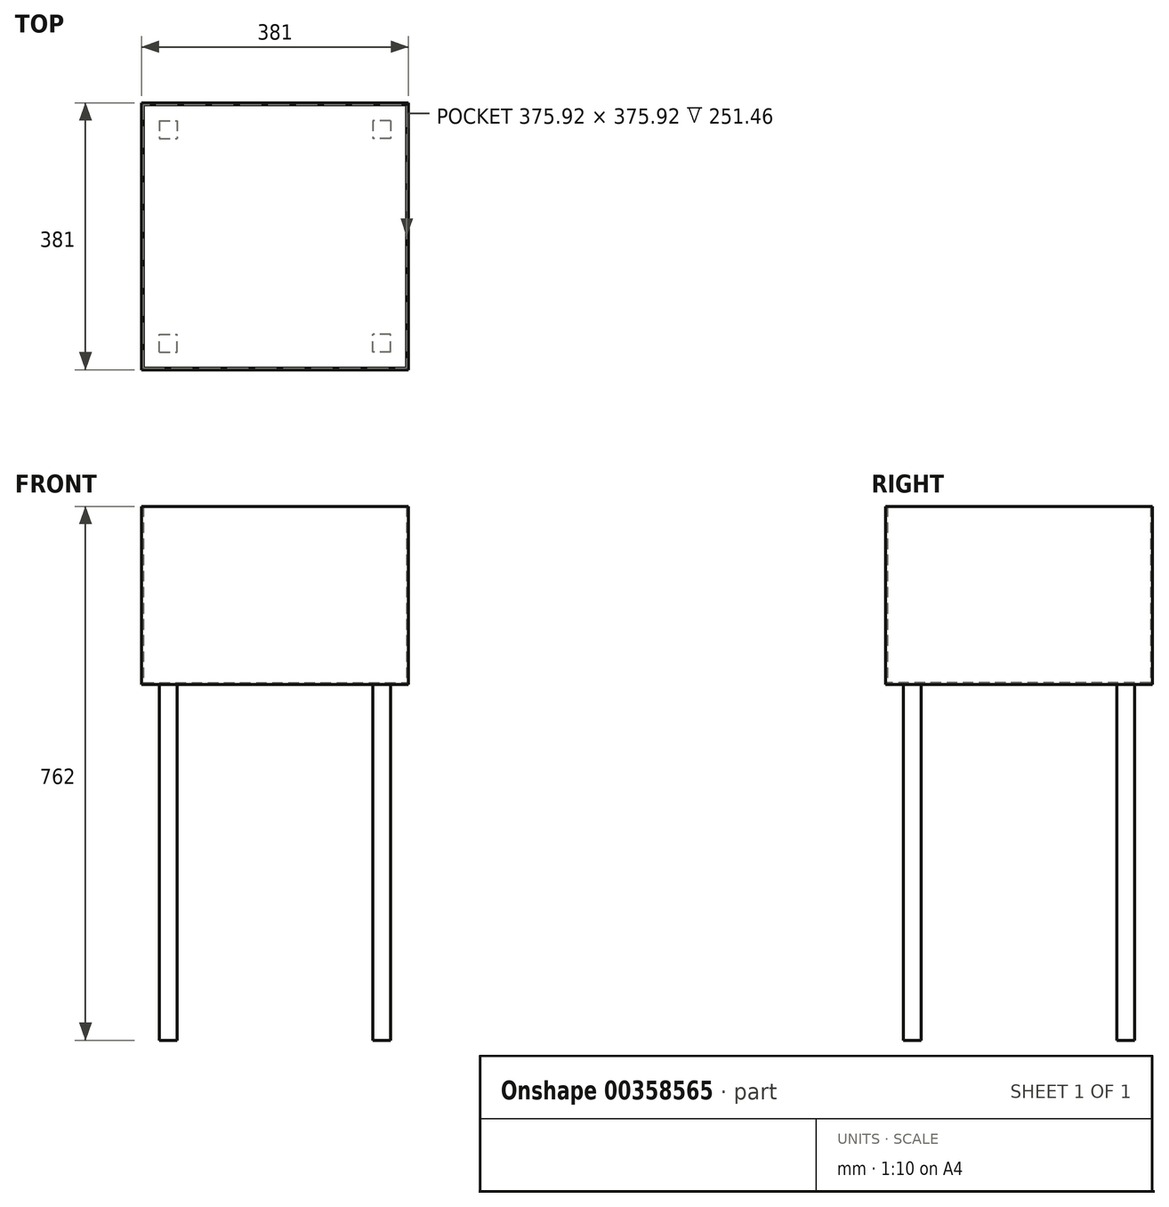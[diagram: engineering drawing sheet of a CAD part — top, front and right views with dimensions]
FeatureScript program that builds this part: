
annotation { "Feature Type Name" : "Feature", "Feature Type Description" : "" }
export const myFeature = defineFeature(function(context is Context, id is Id, definition is map)
    precondition{}
    {
        {
            var Q0;
            Q0=qCreatedBy(makeId("Top.planeOp"),FACE);
            var sketch = newSketch(context, id + "F0", { "sketchPlane" : qUnion([Q0])});
            skLineSegment(sketch, "E0.bottom", {"start": v(0, 0) * mm, "end": v(381, 0) * mm});
            skLineSegment(sketch, "E0.top", {"start": v(0, -381) * mm, "end": v(381, -381) * mm});
            skLineSegment(sketch, "E0.left", {"start": v(0, 0) * mm, "end": v(0, -381) * mm});
            skLineSegment(sketch, "E0.right", {"start": v(381, 0) * mm, "end": v(381, -381) * mm});
            skSolve(sketch);
        }
        {
            var Q0;
            Q0 = qSketchRegion(id + "F0", true);
            extrude(context, id + "F1", {"entities" : qUnion([Q0]), "depth" : 254 * mm});
        }
        {
            var Q0;
            Q0=makeQuery(id+"F1.opExtrude","CAP_FACE",FACE,{"disambiguationData":[OSD([sQuery(id+"F0.wireOp",EDGE,"E0.bottom"),sQuery(id+"F0.wireOp",EDGE,"E0.top"),sQuery(id+"F0.wireOp",EDGE,"E0.left"),sQuery(id+"F0.wireOp",EDGE,"E0.right")])],"isStart":false});
            shell(context, id + "F2", {"entities" : qUnion([Q0]), "thickness" : 2.54 * mm});
        }
        {
            var Q0;
            Q0=makeQuery(id+"F1.opExtrude","CAP_FACE",FACE,{"disambiguationData":[OSD([sQuery(id+"F0.wireOp",EDGE,"E0.bottom"),sQuery(id+"F0.wireOp",EDGE,"E0.top"),sQuery(id+"F0.wireOp",EDGE,"E0.left"),sQuery(id+"F0.wireOp",EDGE,"E0.right")])],"isStart":true});
            var sketch = newSketch(context, id + "F3", { "sketchPlane" : qUnion([Q0])});
            skLineSegment(sketch, "E1.bottom", {"start": v(25.4, 355.6) * mm, "end": v(50.8, 355.6) * mm});
            skLineSegment(sketch, "E1.top", {"start": v(25.4, 330.2) * mm, "end": v(50.8, 330.2) * mm});
            skLineSegment(sketch, "E1.left", {"start": v(25.4, 355.6) * mm, "end": v(25.4, 330.2) * mm});
            skLineSegment(sketch, "E1.right", {"start": v(50.8, 355.6) * mm, "end": v(50.8, 330.2) * mm});
            skLineSegment(sketch, "E2", {"start": v(190.5, 381) * mm, "end": v(190.5, 0) * mm});
            skLineSegment(sketch, "E3", {"start": v(190.5, 0) * mm, "end": v(0, 190.5) * mm});
            skLineSegment(sketch, "E4", {"start": v(0, 190.5) * mm, "end": v(381, 190.5) * mm});
            skLineSegment(sketch, "E5.MirrorCS", {"start": v(355.6, 355.6) * mm, "end": v(330.2, 355.6) * mm});
            skLineSegment(sketch, "E6.MirrorCS", {"start": v(355.6, 330.2) * mm, "end": v(330.2, 330.2) * mm});
            skLineSegment(sketch, "E7.MirrorCS", {"start": v(355.6, 355.6) * mm, "end": v(355.6, 330.2) * mm});
            skLineSegment(sketch, "E8.MirrorCS", {"start": v(330.2, 355.6) * mm, "end": v(330.2, 330.2) * mm});
            skLineSegment(sketch, "E9.MirrorCS", {"start": v(381, 190.5) * mm, "end": v(0, 190.5) * mm});
            skLineSegment(sketch, "E10.MirrorCS", {"start": v(25.4, 25.4) * mm, "end": v(50.8, 25.4) * mm});
            skLineSegment(sketch, "E11.MirrorCS", {"start": v(25.4, 50.8) * mm, "end": v(50.8, 50.8) * mm});
            skLineSegment(sketch, "E12.MirrorCS", {"start": v(25.4, 25.4) * mm, "end": v(25.4, 50.8) * mm});
            skLineSegment(sketch, "E13.MirrorCS", {"start": v(50.8, 25.4) * mm, "end": v(50.8, 50.8) * mm});
            skLineSegment(sketch, "E14.MirrorCS", {"start": v(190.5, 0) * mm, "end": v(190.5, 381) * mm});
            skLineSegment(sketch, "E15.MirrorCS", {"start": v(330.2, 25.4) * mm, "end": v(330.2, 50.8) * mm});
            skLineSegment(sketch, "E16.MirrorCS", {"start": v(355.6, 25.4) * mm, "end": v(330.2, 25.4) * mm});
            skLineSegment(sketch, "E17.MirrorCS", {"start": v(355.6, 50.8) * mm, "end": v(330.2, 50.8) * mm});
            skLineSegment(sketch, "E18.MirrorCS", {"start": v(355.6, 25.4) * mm, "end": v(355.6, 50.8) * mm});
            skSolve(sketch);
        }
        {
            var Q0;
            Q0=makeQuery(id+"F3.imprint","IMPRINT",FACE,{"disambiguationData":[TD([[makeQuery(id+"F3.imprint","IMPRINT",EDGE,{"derivedFrom":sQuery(id+"F3.wireOp",EDGE,"E1.bottom")}),-1.0]])]});
            var Q1;
            Q1=makeQuery(id+"F3.imprint","IMPRINT",FACE,{"disambiguationData":[TD([[makeQuery(id+"F3.imprint","IMPRINT",EDGE,{"derivedFrom":sQuery(id+"F3.wireOp",EDGE,"E5.MirrorCS")}),1.0]])]});
            var Q2;
            Q2=makeQuery(id+"F3.imprint","IMPRINT",FACE,{"disambiguationData":[TD([[makeQuery(id+"F3.imprint","IMPRINT",EDGE,{"derivedFrom":sQuery(id+"F3.wireOp",EDGE,"E10.MirrorCS")}),1.0]])]});
            var Q3;
            Q3=makeQuery(id+"F3.imprint","IMPRINT",FACE,{"disambiguationData":[TD([[makeQuery(id+"F3.imprint","IMPRINT",EDGE,{"derivedFrom":sQuery(id+"F3.wireOp",EDGE,"E15.MirrorCS")}),-1.0]])]});
            extrude(context, id + "F4", {"entities" : qUnion([Q0, Q1, Q2, Q3]), "operationType" : NewBodyOperationType.ADD, "depth" : 508 * mm});
        }
    });
